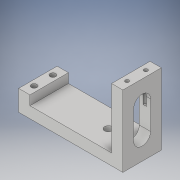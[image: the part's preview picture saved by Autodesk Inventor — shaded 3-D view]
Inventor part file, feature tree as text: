
AUTODESK INVENTOR PART (.ipt)
format: ipt  version: 2019 (Build 230136000, 136)  size: 155,136 bytes
history: native  units: mm
features: extrude x5, sketch x5, other x1
ambient origin geometry x8: Origin, YZ Plane, XZ Plane, XY Plane, X Axis, Y Axis, Z Axis, Center Point
bodies: Body1 (feature_tree)
feature tree (11):
  other  "Твердое тело1"
  extrude  "Выдавливание1"  Depth=38.0mm
  extrude  "Выдавливание2"  Depth=6.0mm
  extrude  "Выдавливание3"  Depth=6.0mm
  extrude  "Выдавливание4"  Depth=6.0mm
  extrude  "Выдавливание5"  Depth=11.0mm
  sketch  "Эскиз1"
  sketch  "Эскиз2"
  sketch  "Эскиз3"
  sketch  "Эскиз4"
  sketch  "Эскиз5"
